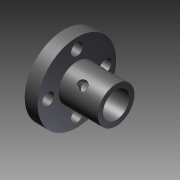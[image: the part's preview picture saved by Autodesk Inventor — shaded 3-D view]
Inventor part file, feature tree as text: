
AUTODESK INVENTOR PART (.ipt)
format: ipt  version: 2016 (Build 200138000, 138)  size: 169,472 bytes
history: native  units: mm
features: other x14, sketch x7, hole x4, revolve x3, thread x2
ambient origin geometry x8: Origin, YZ Plane, XZ Plane, XY Plane, X Axis, Y Axis, Z Axis, Center Point
bodies: Solid1 (feature_tree)
feature tree (30):
  revolve  "Revolution1"  Angle=360.0deg
  revolve  "Revolution2"  Angle=360.0deg
  thread  "Thread1"  [1 undecoded]
  hole  "Hole1"  [1 undecoded]
  hole  "Hole2"  [1 undecoded]
  hole  "Hole3"  [1 undecoded]
  hole  "Hole4"  [1 undecoded]
  revolve  "Revolution3"  [1 undecoded]
  thread  "Thread2"  [1 undecoded]
  other  "to_screw1_XY"
  other  "to_screw1_YZ"
  other  "to_screw1_ZX"
  other  "to_screw1_X"
  other  "to_screw1_Y"
  other  "to_screw1_Z"
  other  "to_screw1_Center"
  other  "to_screw2_XY"
  other  "to_screw2_YZ"
  other  "to_screw2_ZX"
  other  "to_screw2_X"
  other  "to_screw2_Y"
  other  "to_screw2_Z"
  other  "to_screw2_Center"
  sketch  "Sketch_1"  dims[d0=360.0deg d1=360.0deg]
  sketch  "Sketch_3"  dims[d4=4.5mm d5=6.0mm d6=4.0mm d7=2.0mm d8=90.0deg d9=5.0mm d10=0.0mm]
  sketch  "Sketch3"  dims[d11=4.5mm d12=6.0mm d13=4.0mm d14=2.0mm d15=90.0deg d16=5.0mm d17=0.0mm]
  sketch  "Sketch4"  dims[d18=4.5mm d19=6.0mm d20=4.0mm d21=2.0mm d22=90.0deg d23=5.0mm d24=0.0mm]
  sketch  "Sketch5"  dims[d25=4.5mm d26=6.0mm d27=4.0mm d28=2.0mm d29=90.0deg d30=5.0mm d31=0.0mm d32=360.0deg d33=2.121mm d34=0.0mm]
  sketch  "Sketch6"
  sketch  "Sketch_2"  dims[d2=2.121mm d3=0.0mm]
note: 7 required parameter values undecoded (feature->parameter linkage not recoverable at this tier; creation-order binding heuristic only, values carry confidence <= 0.55)
